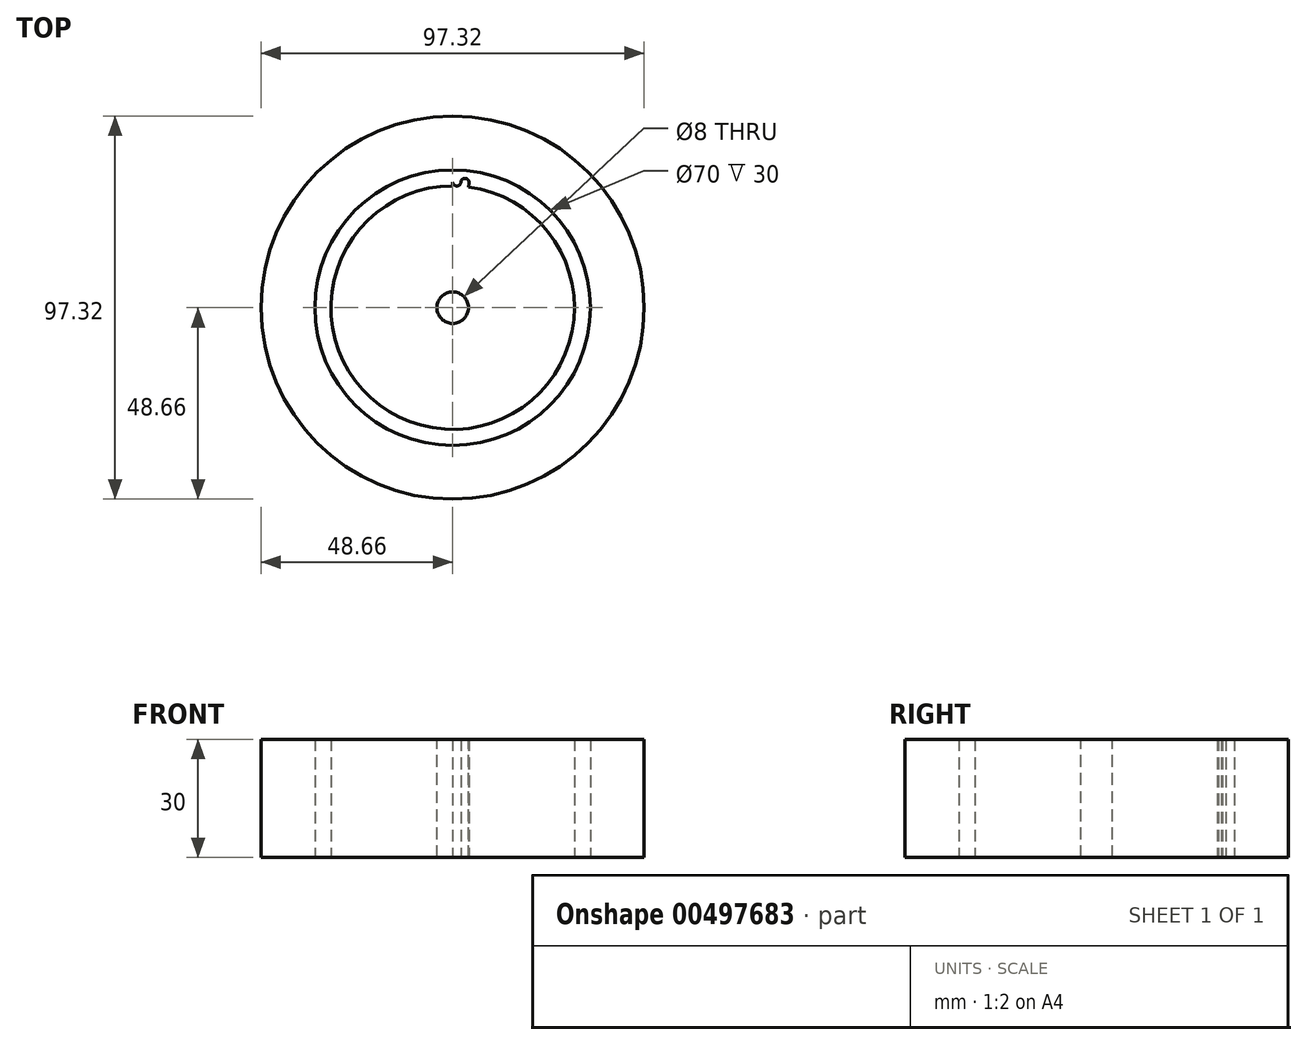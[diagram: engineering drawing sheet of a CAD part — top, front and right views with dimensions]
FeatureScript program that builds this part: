
annotation { "Feature Type Name" : "Feature", "Feature Type Description" : "" }
export const myFeature = defineFeature(function(context is Context, id is Id, definition is map)
    precondition{}
    {
        {
            var Q0;
            Q0=qCreatedBy(makeId("Top.planeOp"),FACE);
            var sketch = newSketch(context, id + "F0", { "sketchPlane" : qUnion([Q0])});
            skCircle(sketch, "E0", {"center": v(0, 0) * mm, "radius": 48.66 * mm});
            skSolve(sketch);
        }
        {
            var Q0;
            Q0=qCreatedBy(makeId("Top.planeOp"),FACE);
            var sketch = newSketch(context, id + "F1", { "sketchPlane" : qUnion([Q0])});
            skCircle(sketch, "E1", {"center": v(0, 0) * mm, "radius": 35 * mm});
            skSolve(sketch);
        }
        {
            var Q0;
            Q0=qCreatedBy(makeId("Top.planeOp"),FACE);
            var sketch = newSketch(context, id + "F2", { "sketchPlane" : qUnion([Q0])});
            skCircle(sketch, "E2", {"center": v(0, 0) * mm, "radius": 30.93 * mm});
            skSolve(sketch);
        }
        {
            var Q0;
            Q0=qCreatedBy(makeId("Top.planeOp"),FACE);
            var sketch = newSketch(context, id + "F3", { "sketchPlane" : qUnion([Q0])});
            skCircle(sketch, "E3", {"center": v(0, 0) * mm, "radius": 4 * mm});
            skSolve(sketch);
        }
        {
            var Q0;
            Q0=qCreatedBy(makeId("Top.planeOp"),FACE);
            var sketch = newSketch(context, id + "F4", { "sketchPlane" : qUnion([Q0])});
            skCircle(sketch, "E4", {"center": v(0, 0) * mm, "radius": 31.97 * mm, "construction": true});
            skArc(sketch, "E5", {"start": v(0, 31.97) * mm, "mid": v(1, 30.92) * mm, "end": v(2.07, 31.9) * mm});
            skArc(sketch, "E6", {"start": v(2.07, 31.9) * mm, "mid": v(3.2, 32.85) * mm, "end": v(4.14, 31.7) * mm});
            skLineSegment(sketch, "E7", {"start": v(4.14, 31.7) * mm, "end": v(0, 0) * mm, "construction": true});
            skLineSegment(sketch, "E8", {"start": v(4.14, 31.7) * mm, "end": v(3.24, 24.85) * mm});
            skLineSegment(sketch, "E9", {"start": v(3.24, 24.85) * mm, "end": v(0, 24.85) * mm});
            skLineSegment(sketch, "E10", {"start": v(0, 24.85) * mm, "end": v(0, 31.97) * mm});
            skSolve(sketch);
        }
        {
            var Q0;
            Q0 = qSketchRegion(id + "F0", true);
            extrude(context, id + "F5", {"entities" : qUnion([Q0]), "depth" : 30 * mm});
        }
        {
            var Q0;
            Q0 = qSketchRegion(id + "F1", true);
            extrude(context, id + "F6", {"entities" : qUnion([Q0]), "operationType" : NewBodyOperationType.REMOVE, "endBound" : BoundingType.THROUGH_ALL, "depth" : 30 * mm, "hasSecondDirection" : true, "secondDirectionBound" : SecondDirectionBoundingType.THROUGH_ALL, "secondDirectionOppositeDirection" : true, "secondDirectionDepth" : 25 * mm});
        }
        {
            var Q0;
            Q0 = qSketchRegion(id + "F2", true);
            extrude(context, id + "F7", {"entities" : qUnion([Q0]), "depth" : 30 * mm});
        }
        {
            var Q0;
            Q0 = qSketchRegion(id + "F3", true);
            extrude(context, id + "F8", {"entities" : qUnion([Q0]), "operationType" : NewBodyOperationType.REMOVE, "endBound" : BoundingType.THROUGH_ALL, "oppositeDirection" : true, "depth" : 25 * mm, "hasSecondDirection" : true, "secondDirectionBound" : SecondDirectionBoundingType.THROUGH_ALL, "secondDirectionOppositeDirection" : false, "secondDirectionDepth" : 25 * mm});
        }
        {
            var Q0;
            Q0 = qSketchRegion(id + "F4", true);
            extrude(context, id + "F9", {"entities" : qUnion([Q0]), "operationType" : NewBodyOperationType.ADD, "depth" : 30 * mm});
        }
    });
